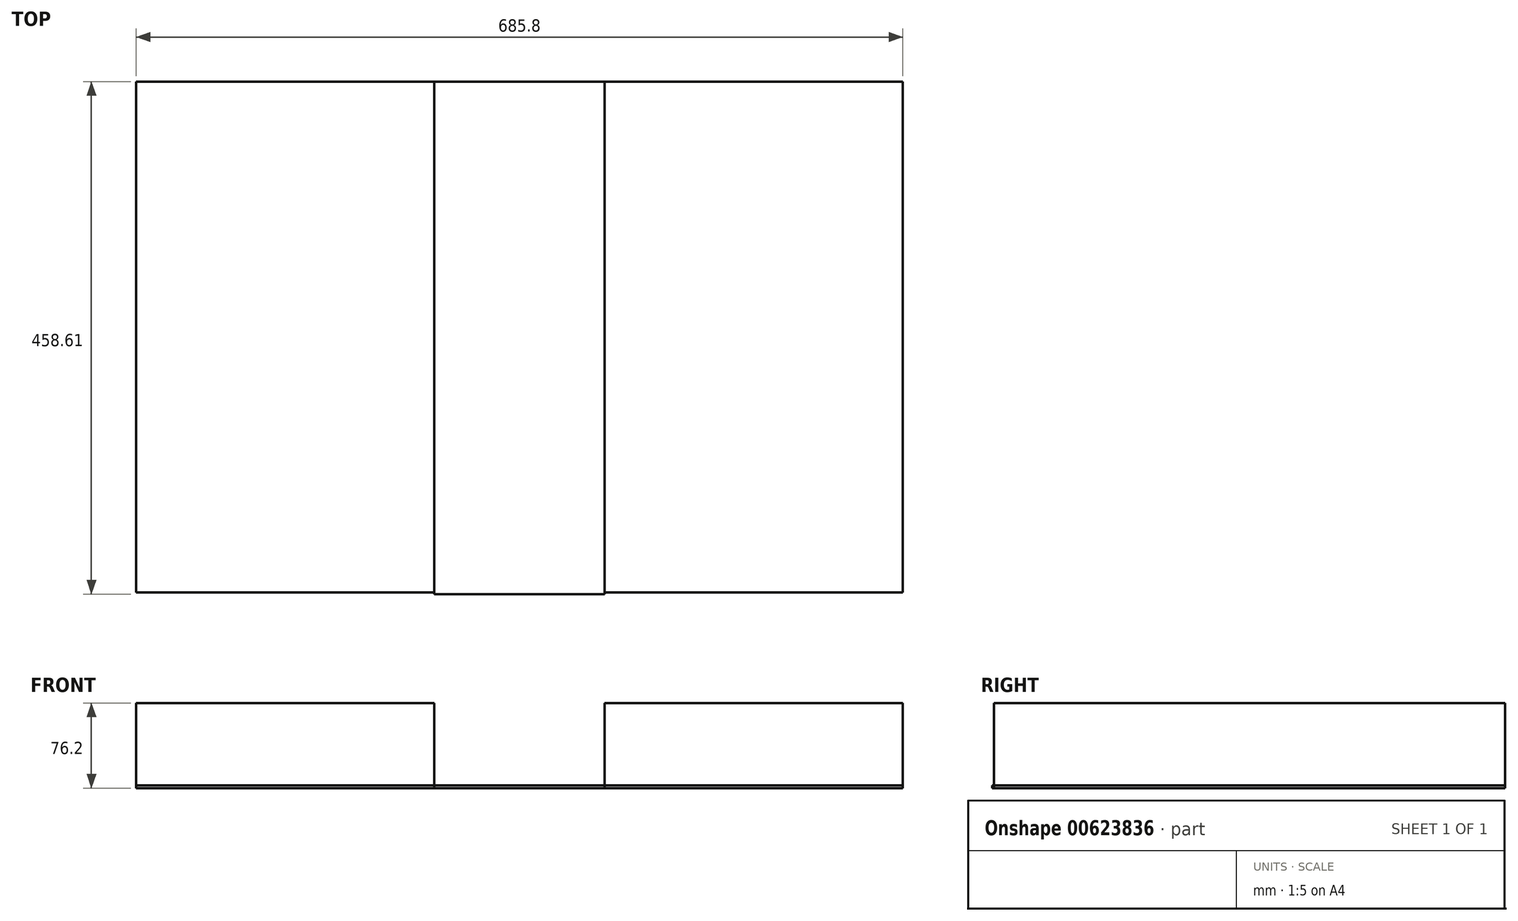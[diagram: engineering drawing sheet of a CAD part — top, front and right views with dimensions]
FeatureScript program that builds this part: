
annotation { "Feature Type Name" : "Feature", "Feature Type Description" : "" }
export const myFeature = defineFeature(function(context is Context, id is Id, definition is map)
    precondition{}
    {
        {
            var Q0;
            Q0=qCreatedBy(makeId("Top.planeOp"),FACE);
            var sketch = newSketch(context, id + "F0", { "sketchPlane" : qUnion([Q0])});
            skLineSegment(sketch, "E0.bottom", {"start": v(-312.67, 264.67) * mm, "end": v(373.13, 264.67) * mm});
            skLineSegment(sketch, "E0.top", {"start": v(-312.67, -192.53) * mm, "end": v(373.13, -192.53) * mm});
            skLineSegment(sketch, "E0.left", {"start": v(-312.67, 264.67) * mm, "end": v(-312.67, -192.53) * mm});
            skLineSegment(sketch, "E0.right", {"start": v(373.13, 264.67) * mm, "end": v(373.13, -192.53) * mm});
            skLineSegment(sketch, "E1.bottom", {"start": v(-45.97, 264.67) * mm, "end": v(106.43, 264.67) * mm});
            skLineSegment(sketch, "E1.top", {"start": v(-45.97, -193.94) * mm, "end": v(106.43, -193.94) * mm});
            skLineSegment(sketch, "E1.left", {"start": v(-45.97, 264.67) * mm, "end": v(-45.97, -193.94) * mm});
            skLineSegment(sketch, "E1.right", {"start": v(106.43, 264.67) * mm, "end": v(106.43, -193.94) * mm});
            skLineSegment(sketch, "E2", {"start": v(-312.67, 110.71) * mm, "end": v(-45.97, 110.71) * mm});
            skSolve(sketch);
        }
        {
            var Q0;
            {var subQ5=sQuery(id+"F0.wireOp",EDGE,"E2");Q0=makeQuery(id+"F0.imprint","IMPRINT",FACE,{"disambiguationData":[TD([[makeQuery(id+"F0.imprint","IMPRINT",EDGE,{"derivedFrom":subQ5}),-1.0]])]});}
            var Q1;
            {var subQ0=sQuery(id+"F0.wireOp",EDGE,"E0.right");Q1=makeQuery(id+"F0.imprint","IMPRINT",FACE,{"disambiguationData":[TD([[makeQuery(id+"F0.imprint","IMPRINT",EDGE,{"derivedFrom":subQ0}),-1.0]])]});}
            var Q2;
            {var subQ5=sQuery(id+"F0.wireOp",EDGE,"E2");Q2=makeQuery(id+"F0.imprint","IMPRINT",FACE,{"disambiguationData":[TD([[makeQuery(id+"F0.imprint","IMPRINT",EDGE,{"derivedFrom":subQ5}),1.0]])]});}
            extrude(context, id + "F1", {"entities" : qUnion([Q0, Q1, Q2]), "depth" : 76.2 * mm, "offsetDistance" : 25.4 * mm});
        }
        {
            var Q0;
            Q0 = qSketchRegion(id + "F0", true);
            extrude(context, id + "F2", {"entities" : qUnion([Q0]), "depth" : 2.54 * mm, "offsetDistance" : 25.4 * mm});
        }
    });
